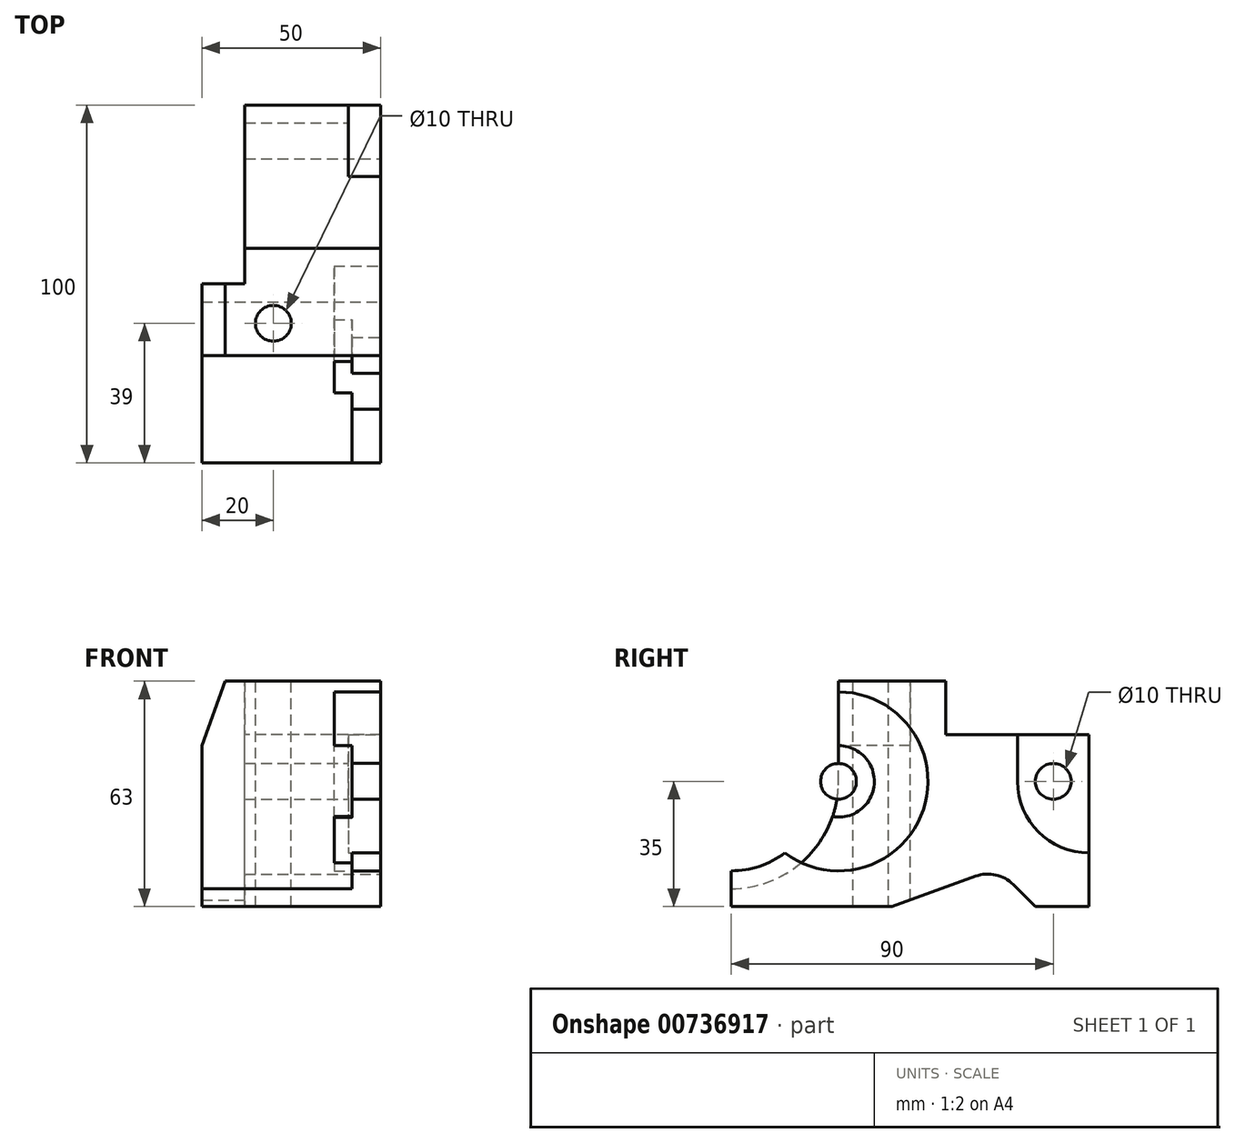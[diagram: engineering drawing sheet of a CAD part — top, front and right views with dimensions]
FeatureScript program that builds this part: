
annotation { "Feature Type Name" : "Feature", "Feature Type Description" : "" }
export const myFeature = defineFeature(function(context is Context, id is Id, definition is map)
    precondition{}
    {
        {
            var Q0;
            Q0=qCreatedBy(makeId("Right.planeOp"),FACE);
            var sketch = newSketch(context, id + "F0", { "sketchPlane" : qUnion([Q0])});
            skLineSegment(sketch, "E0.bottom", {"start": v(-30, 28) * mm, "end": v(70, 28) * mm});
            skLineSegment(sketch, "E0.top", {"start": v(-30, -35) * mm, "end": v(70, -35) * mm});
            skLineSegment(sketch, "E0.left", {"start": v(-30, 28) * mm, "end": v(-30, -35) * mm});
            skLineSegment(sketch, "E0.right", {"start": v(70, 28) * mm, "end": v(70, -35) * mm});
            skLineSegment(sketch, "E1", {"start": v(30, 28) * mm, "end": v(30, 13) * mm});
            skLineSegment(sketch, "E2", {"start": v(30, 13) * mm, "end": v(70, 13) * mm});
            skSolve(sketch);
        }
        {
            var Q0;
            {var subQ1=sQuery(id+"F0.wireOp",EDGE,"E0.top");Q0=makeQuery(id+"F0.imprint","IMPRINT",FACE,{"disambiguationData":[TD([[makeQuery(id+"F0.imprint","IMPRINT",EDGE,{"derivedFrom":subQ1}),1.0]])]});}
            extrude(context, id + "F1", {"entities" : qUnion([Q0]), "depth" : 50 * mm, "offsetDistance" : 25 * mm});
        }
        {
            var Q0;
            Q0=makeQuery(id+"F1.opExtrude","SWEPT_FACE",FACE,{"disambiguationData":[OSD([sQuery(id+"F0.wireOp",EDGE,"E0.bottom")])]});
            var sketch = newSketch(context, id + "F2", { "sketchPlane" : qUnion([Q0])});
            skLineSegment(sketch, "E3", {"start": v(0, 20) * mm, "end": v(12, 20) * mm});
            skLineSegment(sketch, "E4.0", {"start": v(12, 70) * mm, "end": v(0, 70) * mm});
            skLineSegment(sketch, "E4.1", {"start": v(0, 20) * mm, "end": v(0, 30) * mm});
            skLineSegment(sketch, "E4.2", {"start": v(0, 30) * mm, "end": v(0, 70) * mm});
            skLineSegment(sketch, "E5", {"start": v(12, 20) * mm, "end": v(12, 70) * mm});
            skPoint(sketch, "E6.orphan", {"position": v(0, -30) * mm});
            skPoint(sketch, "E7.orphan", {"position": v(50, 70) * mm});
            skSolve(sketch);
        }
        {
            var Q0;
            Q0 = qSketchRegion(id + "F2", true);
            extrude(context, id + "F3", {"entities" : qUnion([Q0]), "operationType" : NewBodyOperationType.REMOVE, "endBound" : BoundingType.THROUGH_ALL, "oppositeDirection" : true, "depth" : 25 * mm, "offsetDistance" : 25 * mm});
        }
        {
            var Q0;
            Q0=makeQuery(id+"F1.opExtrude","SWEPT_FACE",FACE,{"disambiguationData":[OSD([sQuery(id+"F0.wireOp",EDGE,"E0.left")])]});
            var sketch = newSketch(context, id + "F4", { "sketchPlane" : qUnion([Q0])});
            skLineSegment(sketch, "E8", {"start": v(6.55, 28) * mm, "end": v(0, 10) * mm});
            skLineSegment(sketch, "E9", {"start": v(0, 10) * mm, "end": v(0, 28) * mm});
            skLineSegment(sketch, "E10", {"start": v(0, 28) * mm, "end": v(6.55, 28) * mm});
            skSolve(sketch);
        }
        {
            var Q0;
            Q0 = qSketchRegion(id + "F4", true);
            extrude(context, id + "F5", {"entities" : qUnion([Q0]), "operationType" : NewBodyOperationType.REMOVE, "endBound" : BoundingType.THROUGH_ALL, "oppositeDirection" : true, "depth" : 25 * mm, "offsetDistance" : 25 * mm});
        }
        {
            var Q0;
            Q0=makeQuery(id+"F1.opExtrude","CAP_FACE",FACE,{"disambiguationData":[OSD([sQuery(id+"F0.wireOp",EDGE,"E0.bottom"),sQuery(id+"F0.wireOp",EDGE,"E0.top"),sQuery(id+"F0.wireOp",EDGE,"E0.left"),sQuery(id+"F0.wireOp",EDGE,"E0.right"),sQuery(id+"F0.wireOp",EDGE,"E1"),sQuery(id+"F0.wireOp",EDGE,"E2")])],"isStart":true});
            var sketch = newSketch(context, id + "F6", { "sketchPlane" : qUnion([Q0])});
            skArc(sketch, "E11", {"start": v(0, 0) * mm, "mid": v(8.79, -21.21) * mm, "end": v(30, -30) * mm});
            skLineSegment(sketch, "E12", {"start": v(0, 0) * mm, "end": v(0, 28) * mm});
            skLineSegment(sketch, "E13", {"start": v(0, 28) * mm, "end": v(19.23, 28) * mm});
            skLineSegment(sketch, "E14.0", {"start": v(0, 28) * mm, "end": v(30, 28) * mm});
            skLineSegment(sketch, "E14.1", {"start": v(30, 28) * mm, "end": v(30, 10) * mm});
            skLineSegment(sketch, "E14.2", {"start": v(30, 10) * mm, "end": v(30, -30) * mm});
            skPoint(sketch, "E15.orphan", {"position": v(-20, 28) * mm});
            skPoint(sketch, "E16.orphan", {"position": v(30, -35) * mm});
            skSolve(sketch);
        }
        {
            var Q0;
            Q0 = qSketchRegion(id + "F6", true);
            extrude(context, id + "F7", {"entities" : qUnion([Q0]), "operationType" : NewBodyOperationType.REMOVE, "oppositeDirection" : true, "depth" : 42 * mm, "offsetDistance" : 25 * mm});
        }
        {
            var Q0;
            Q0=makeQuery(id+"F1.opExtrude","CAP_FACE",FACE,{"disambiguationData":[OSD([sQuery(id+"F0.wireOp",EDGE,"E0.bottom"),sQuery(id+"F0.wireOp",EDGE,"E0.top"),sQuery(id+"F0.wireOp",EDGE,"E0.left"),sQuery(id+"F0.wireOp",EDGE,"E0.right"),sQuery(id+"F0.wireOp",EDGE,"E1"),sQuery(id+"F0.wireOp",EDGE,"E2")])],"isStart":false});
            var sketch = newSketch(context, id + "F8", { "sketchPlane" : qUnion([Q0])});
            skCircle(sketch, "E17", {"center": v(0, 0) * mm, "radius": 25 * mm});
            skCircle(sketch, "E18", {"center": v(0, 0) * mm, "radius": 10 * mm});
            skSolve(sketch);
        }
        {
            var Q0;
            Q0 = qSketchRegion(id + "F8", true);
            extrude(context, id + "F9", {"entities" : qUnion([Q0]), "operationType" : NewBodyOperationType.REMOVE, "oppositeDirection" : true, "depth" : 13 * mm, "offsetDistance" : 25 * mm});
        }
        {
            var Q0;
            Q0=makeQuery(id+"F9.boolean.opBoolean","SPLIT",FACE,{"disambiguationData":[TD([makeQuery(id+"F9.opExtrude","SWEPT_FACE",FACE,{"disambiguationData":[OSD([sQuery(id+"F8.wireOp",EDGE,"E18")])]})])],"derivedFrom":makeQuery(id+"F1.opExtrude","CAP_FACE",FACE,{"disambiguationData":[OSD([sQuery(id+"F0.wireOp",EDGE,"E0.bottom"),sQuery(id+"F0.wireOp",EDGE,"E0.top"),sQuery(id+"F0.wireOp",EDGE,"E0.left"),sQuery(id+"F0.wireOp",EDGE,"E0.right"),sQuery(id+"F0.wireOp",EDGE,"E1"),sQuery(id+"F0.wireOp",EDGE,"E2")])],"isStart":false})});
            var sketch = newSketch(context, id + "F10", { "sketchPlane" : qUnion([Q0])});
            skCircle(sketch, "E19", {"center": v(0, 0) * mm, "radius": 5 * mm});
            skCircle(sketch, "E20.0", {"center": v(0, 0) * mm, "radius": 10 * mm});
            skSolve(sketch);
        }
        {
            var Q0;
            Q0 = qSketchRegion(id + "F10", true);
            extrude(context, id + "F11", {"entities" : qUnion([Q0]), "operationType" : NewBodyOperationType.REMOVE, "oppositeDirection" : true, "depth" : 8 * mm, "offsetDistance" : 25 * mm});
        }
        {
            var Q0;
            {var subQ0=sQuery(id+"F0.wireOp",EDGE,"E0.left");var subQ1=sQuery(id+"F0.wireOp",EDGE,"E0.top");var subQ2=sQuery(id+"F0.wireOp",EDGE,"E0.right");var subQ3=sQuery(id+"F0.wireOp",EDGE,"E0.bottom");var subQ4=sQuery(id+"F0.wireOp",EDGE,"E1");var subQ5=sQuery(id+"F0.wireOp",EDGE,"E2");Q0=makeQuery(id+"F9.boolean.opBoolean","SPLIT",FACE,{"disambiguationData":[TD([makeQuery(id+"F1.opExtrude","SWEPT_FACE",FACE,{"disambiguationData":[OSD([subQ3])]})])],"derivedFrom":makeQuery(id+"F1.opExtrude","CAP_FACE",FACE,{"disambiguationData":[OSD([subQ3,subQ1,subQ0,subQ2,subQ4,subQ5])],"isStart":false})});}
            var sketch = newSketch(context, id + "F12", { "sketchPlane" : qUnion([Q0])});
            skArc(sketch, "E21", {"start": v(-30, -25) * mm, "mid": v(-19.18, -22.54) * mm, "end": v(-10.5, -15.64) * mm});
            skLineSegment(sketch, "E22", {"start": v(-10.5, -15.64) * mm, "end": v(-10.5, 7.6) * mm});
            skLineSegment(sketch, "E23", {"start": v(-10.5, 7.6) * mm, "end": v(0, 25) * mm});
            skLineSegment(sketch, "E24", {"start": v(0, 25) * mm, "end": v(0, 28) * mm});
            skLineSegment(sketch, "E25", {"start": v(0, 28) * mm, "end": v(-30, 28) * mm});
            skLineSegment(sketch, "E26", {"start": v(-30, 28) * mm, "end": v(-30, -25) * mm});
            skSolve(sketch);
        }
        {
            var Q0;
            Q0 = qSketchRegion(id + "F12", true);
            extrude(context, id + "F13", {"entities" : qUnion([Q0]), "operationType" : NewBodyOperationType.REMOVE, "oppositeDirection" : true, "depth" : 25 * mm, "offsetDistance" : 25 * mm});
        }
        {
            var Q0;
            {var subQ0=sQuery(id+"F0.wireOp",EDGE,"E0.left");var subQ1=sQuery(id+"F0.wireOp",EDGE,"E0.top");var subQ2=sQuery(id+"F0.wireOp",EDGE,"E0.right");var subQ3=sQuery(id+"F0.wireOp",EDGE,"E0.bottom");var subQ4=sQuery(id+"F0.wireOp",EDGE,"E1");var subQ5=sQuery(id+"F0.wireOp",EDGE,"E2");Q0=makeQuery(id+"F9.boolean.opBoolean","SPLIT",FACE,{"disambiguationData":[TD([makeQuery(id+"F1.opExtrude","SWEPT_FACE",FACE,{"disambiguationData":[OSD([subQ3])]})])],"derivedFrom":makeQuery(id+"F1.opExtrude","CAP_FACE",FACE,{"disambiguationData":[OSD([subQ3,subQ1,subQ0,subQ2,subQ4,subQ5])],"isStart":false})});}
            var sketch = newSketch(context, id + "F14", { "sketchPlane" : qUnion([Q0])});
            skLineSegment(sketch, "E27", {"start": v(15, -35) * mm, "end": v(38.34, -26.5) * mm});
            skLineSegment(sketch, "E28", {"start": v(48.83, -28.83) * mm, "end": v(55, -35) * mm});
            skLineSegment(sketch, "E29", {"start": v(55, -35) * mm, "end": v(15, -35) * mm});
            skPoint(sketch, "E30.visualSharp", {"position": v(44.33, -24.33) * mm});
            skArc(sketch, "E30.filletArc", {"start": v(48.83, -28.83) * mm, "mid": v(43.92, -26.14) * mm, "end": v(38.34, -26.5) * mm});
            skSolve(sketch);
        }
        {
            var Q0;
            Q0 = qSketchRegion(id + "F14", true);
            extrude(context, id + "F15", {"entities" : qUnion([Q0]), "operationType" : NewBodyOperationType.REMOVE, "endBound" : BoundingType.THROUGH_ALL, "oppositeDirection" : true, "depth" : 25 * mm, "offsetDistance" : 25 * mm});
        }
        {
            var Q0;
            {var subQ0=sQuery(id+"F0.wireOp",EDGE,"E0.left");var subQ1=sQuery(id+"F0.wireOp",EDGE,"E0.top");var subQ2=sQuery(id+"F0.wireOp",EDGE,"E0.right");var subQ3=sQuery(id+"F0.wireOp",EDGE,"E0.bottom");var subQ4=sQuery(id+"F0.wireOp",EDGE,"E1");var subQ5=sQuery(id+"F0.wireOp",EDGE,"E2");Q0=makeQuery(id+"F9.boolean.opBoolean","SPLIT",FACE,{"disambiguationData":[TD([makeQuery(id+"F1.opExtrude","SWEPT_FACE",FACE,{"disambiguationData":[OSD([subQ3])]})])],"derivedFrom":makeQuery(id+"F1.opExtrude","CAP_FACE",FACE,{"disambiguationData":[OSD([subQ3,subQ1,subQ0,subQ2,subQ4,subQ5])],"isStart":false})});}
            var sketch = newSketch(context, id + "F16", { "sketchPlane" : qUnion([Q0])});
            skArc(sketch, "E31", {"start": v(50, 0) * mm, "mid": v(55.86, -14.14) * mm, "end": v(70, -20) * mm});
            skLineSegment(sketch, "E32", {"start": v(50, 0) * mm, "end": v(50, 13) * mm});
            skLineSegment(sketch, "E33", {"start": v(50, 13) * mm, "end": v(70, 13) * mm});
            skLineSegment(sketch, "E34", {"start": v(70, 13) * mm, "end": v(70, -20) * mm});
            skSolve(sketch);
        }
        {
            var Q0;
            Q0 = qSketchRegion(id + "F16", true);
            extrude(context, id + "F17", {"entities" : qUnion([Q0]), "operationType" : NewBodyOperationType.REMOVE, "oppositeDirection" : true, "depth" : 9 * mm, "offsetDistance" : 25 * mm});
        }
        {
            var Q0;
            Q0=makeQuery(id+"F17.boolean.opBoolean","COPY",FACE,{"derivedFrom":makeQuery(id+"F17.opExtrude","CAP_FACE",FACE,{"disambiguationData":[OSD([sQuery(id+"F16.wireOp",EDGE,"E31"),sQuery(id+"F16.wireOp",EDGE,"E32"),sQuery(id+"F16.wireOp",EDGE,"E33"),sQuery(id+"F16.wireOp",EDGE,"E34")])],"isStart":false})});
            var sketch = newSketch(context, id + "F18", { "sketchPlane" : qUnion([Q0])});
            skCircle(sketch, "E35", {"center": v(60, 0) * mm, "radius": 5 * mm});
            skSolve(sketch);
        }
        {
            var Q0;
            Q0 = qSketchRegion(id + "F18", true);
            extrude(context, id + "F19", {"entities" : qUnion([Q0]), "operationType" : NewBodyOperationType.REMOVE, "endBound" : BoundingType.THROUGH_ALL, "oppositeDirection" : true, "depth" : 25 * mm, "offsetDistance" : 25 * mm});
        }
        {
            var Q0;
            Q0=makeQuery(id+"F1.opExtrude","SWEPT_FACE",FACE,{"disambiguationData":[OSD([sQuery(id+"F0.wireOp",EDGE,"E0.bottom")])]});
            var sketch = newSketch(context, id + "F20", { "sketchPlane" : qUnion([Q0])});
            skCircle(sketch, "E36", {"center": v(20, 9) * mm, "radius": 5 * mm});
            skSolve(sketch);
        }
        {
            var Q0;
            Q0 = qSketchRegion(id + "F20", true);
            extrude(context, id + "F21", {"entities" : qUnion([Q0]), "operationType" : NewBodyOperationType.REMOVE, "endBound" : BoundingType.THROUGH_ALL, "oppositeDirection" : true, "depth" : 25 * mm, "offsetDistance" : 25 * mm});
        }
    });
